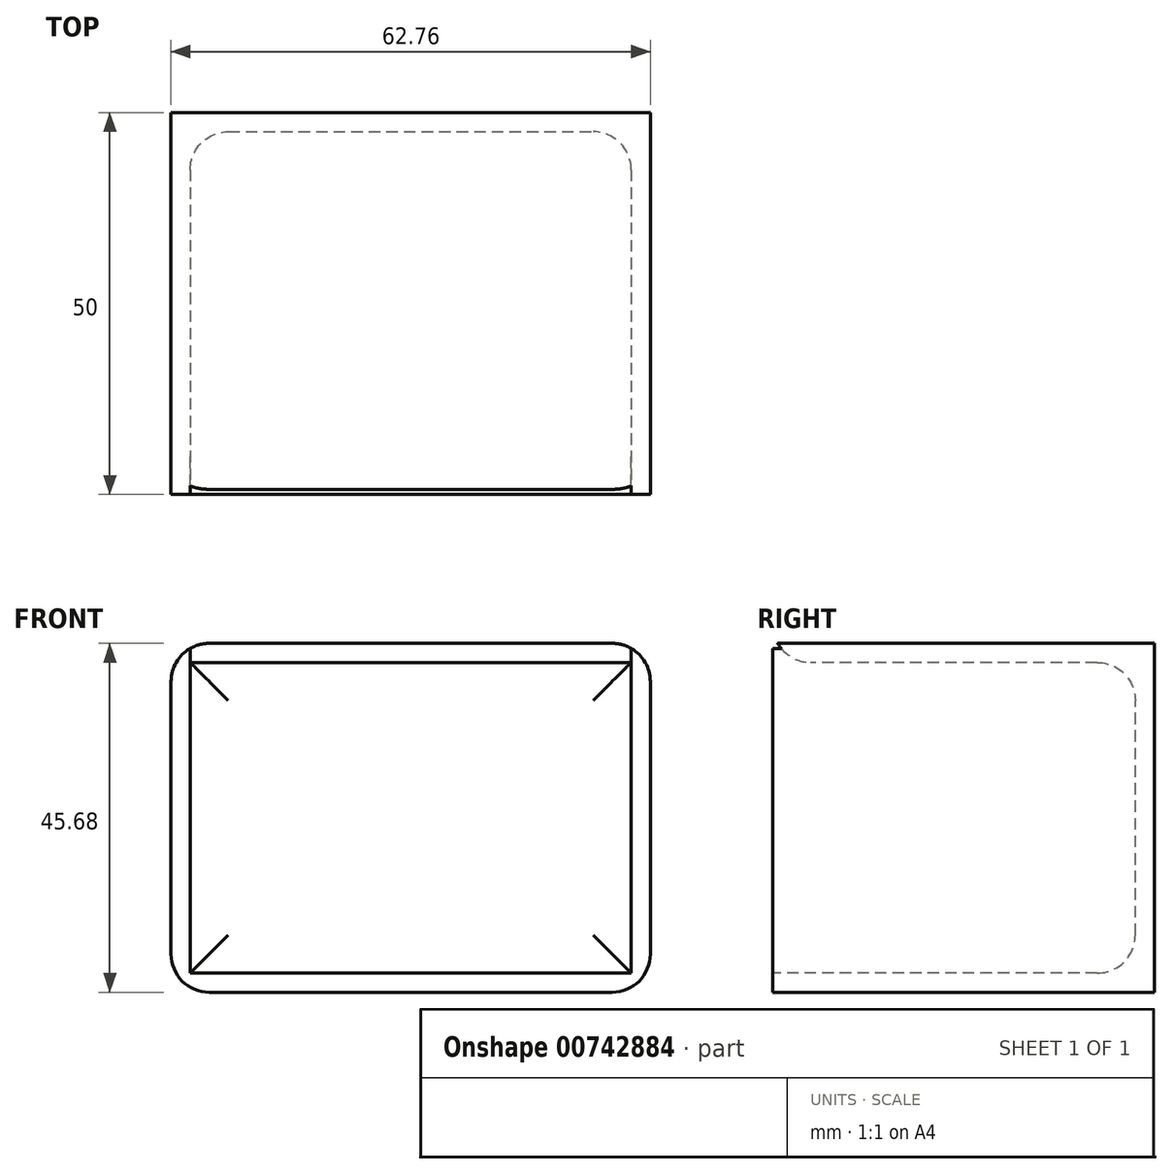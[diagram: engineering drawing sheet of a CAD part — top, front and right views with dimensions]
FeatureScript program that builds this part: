
annotation { "Feature Type Name" : "Feature", "Feature Type Description" : "" }
export const myFeature = defineFeature(function(context is Context, id is Id, definition is map)
    precondition{}
    {
        {
            var Q0;
            Q0=qCreatedBy(makeId("Front.planeOp"),FACE);
            var sketch = newSketch(context, id + "F0", { "sketchPlane" : qUnion([Q0])});
            skLineSegment(sketch, "E0.bottom", {"start": v(0, 0) * mm, "end": v(62.76, 0) * mm});
            skLineSegment(sketch, "E0.top", {"start": v(0, 45.68) * mm, "end": v(62.76, 45.68) * mm});
            skLineSegment(sketch, "E0.left", {"start": v(0, 0) * mm, "end": v(0, 45.68) * mm});
            skLineSegment(sketch, "E0.right", {"start": v(62.76, 0) * mm, "end": v(62.76, 45.68) * mm});
            skSolve(sketch);
        }
        {
            var Q0;
            Q0=makeQuery(id+"F0.imprint","IMPRINT",FACE,{"disambiguationData":[TD([[makeQuery(id+"F0.imprint","IMPRINT",EDGE,{"derivedFrom":sQuery(id+"F0.wireOp",EDGE,"E0.bottom")}),1.0]])]});
            extrude(context, id + "F1", {"entities" : qUnion([Q0]), "oppositeDirection" : true, "depth" : 50 * mm, "offsetDistance" : 25 * mm});
        }
        {
            var Q0;
            Q0=makeQuery(id+"F1.opExtrude","CAP_FACE",FACE,{"disambiguationData":[OSD([sQuery(id+"F0.wireOp",EDGE,"E0.bottom"),sQuery(id+"F0.wireOp",EDGE,"E0.top"),sQuery(id+"F0.wireOp",EDGE,"E0.left"),sQuery(id+"F0.wireOp",EDGE,"E0.right")])],"isStart":true});
            shell(context, id + "F2", {"entities" : qUnion([Q0]), "thickness" : 2.5 * mm});
        }
        {
            var Q0;
            Q0=makeQuery(id+"F1.opExtrude","SWEPT_EDGE",EDGE,{"disambiguationData":[OSD([sQuery(id+"F0.wireOp",EDGE,"E0.top"),sQuery(id+"F0.wireOp",EDGE,"E0.left")])]});
            var Q1;
            Q1=makeQuery(id+"F1.opExtrude","SWEPT_EDGE",EDGE,{"disambiguationData":[OSD([sQuery(id+"F0.wireOp",EDGE,"E0.top"),sQuery(id+"F0.wireOp",EDGE,"E0.right")])]});
            var Q2;
            Q2=makeQuery(id+"F1.opExtrude","SWEPT_EDGE",EDGE,{"disambiguationData":[OSD([sQuery(id+"F0.wireOp",EDGE,"E0.bottom"),sQuery(id+"F0.wireOp",EDGE,"E0.right")])]});
            var Q3;
            Q3=makeQuery(id+"F1.opExtrude","SWEPT_EDGE",EDGE,{"disambiguationData":[OSD([sQuery(id+"F0.wireOp",EDGE,"E0.bottom"),sQuery(id+"F0.wireOp",EDGE,"E0.left")])]});
            fillet(context, id + "F3", {"entities" : qUnion([Q0, Q1, Q2, Q3]), "radius" : 5 * mm, "tangentPropagation" : true, "allowEdgeOverflow" : false});
        }
        {
            var Q0;
            {var subQ0=sQuery(id+"F0.wireOp",EDGE,"E0.top");Q0=makeQuery(id+"F2.opShell","OFFSET_EDGE",EDGE,{"disambiguationData":[OSD([subQ0]),TDD([makeQuery(id+"F1.opExtrude","CAP_EDGE",EDGE,{"disambiguationData":[OSD([subQ0])],"isStart":true})])]});}
            var Q1;
            Q1=makeQuery(id+"F2.opShell","OFFSET_FACE",FACE,{"disambiguationData":[OSD([sQuery(id+"F0.wireOp",EDGE,"E0.bottom"),sQuery(id+"F0.wireOp",EDGE,"E0.top"),sQuery(id+"F0.wireOp",EDGE,"E0.left"),sQuery(id+"F0.wireOp",EDGE,"E0.right")])]});
            fillet(context, id + "F4", {"entities" : qUnion([Q0, Q1]), "radius" : 5 * mm, "tangentPropagation" : true, "allowEdgeOverflow" : false});
        }
    });
